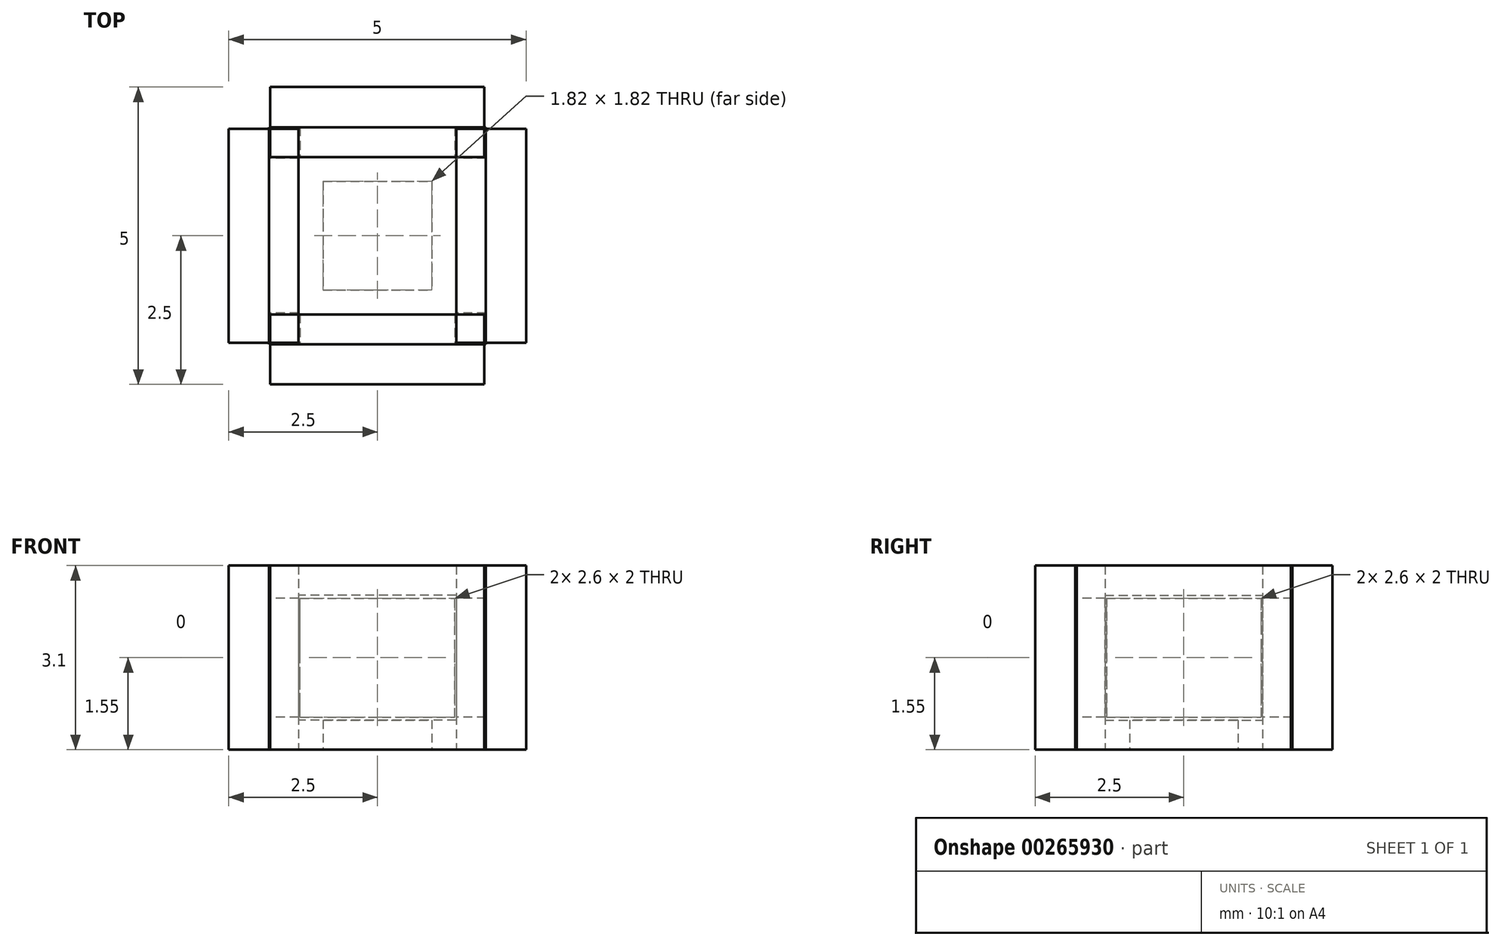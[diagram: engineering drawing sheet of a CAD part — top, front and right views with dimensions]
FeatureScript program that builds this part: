
annotation { "Feature Type Name" : "Feature", "Feature Type Description" : "" }
export const myFeature = defineFeature(function(context is Context, id is Id, definition is map)
    precondition{}
    {
        {
            var Q0;
            Q0=qCreatedBy(makeId("Top.planeOp"),FACE);
            var sketch = newSketch(context, id + "F0", { "sketchPlane" : qUnion([Q0])});
            skLineSegment(sketch, "E0.bottom", {"start": v(1.82, -1.82) * mm, "end": v(-1.82, -1.83) * mm});
            skLineSegment(sketch, "E0.top", {"start": v(1.83, 1.83) * mm, "end": v(-1.82, 1.82) * mm});
            skLineSegment(sketch, "E0.left", {"start": v(1.82, -1.82) * mm, "end": v(1.83, 1.83) * mm});
            skLineSegment(sketch, "E0.right", {"start": v(-1.82, -1.83) * mm, "end": v(-1.82, 1.82) * mm});
            skPoint(sketch, "E0.middle", {"position": v(0, 0) * mm});
            skSolve(sketch);
        }
        {
            var Q0;
            Q0=qSketchRegion(id+"F0",true);
            extrude(context, id + "F1", {"entities" : qUnion([Q0]), "depth" : 3.1 * mm});
        }
        {
            var Q0;
            Q0=qCreatedBy(makeId("Top.planeOp"),FACE);
            var sketch = newSketch(context, id + "F2", { "sketchPlane" : qUnion([Q0])});
            skLineSegment(sketch, "E1.bottom", {"start": v(1.33, -1.32) * mm, "end": v(-1.32, -1.32) * mm});
            skLineSegment(sketch, "E1.top", {"start": v(1.32, 1.32) * mm, "end": v(-1.33, 1.32) * mm});
            skLineSegment(sketch, "E1.left", {"start": v(1.32, -1.32) * mm, "end": v(1.32, 1.33) * mm});
            skLineSegment(sketch, "E1.right", {"start": v(-1.32, -1.32) * mm, "end": v(-1.33, 1.33) * mm});
            skPoint(sketch, "E1.middle", {"position": v(0, 0) * mm});
            skSolve(sketch);
        }
        {
            var Q0;
            Q0=qSketchRegion(id+"F2",true);
            extrude(context, id + "F3", {"entities" : qUnion([Q0]), "depth" : 2.1 * mm});
        }
        {
            var Q0;
            Q0=makeQuery(id+"F3.opExtrude","SWEPT_BODY",BODY,{"disambiguationData":[OSD([sQuery(id+"F2.wireOp",EDGE,"E1.bottom"),sQuery(id+"F2.wireOp",EDGE,"E1.top"),sQuery(id+"F2.wireOp",EDGE,"E1.left"),sQuery(id+"F2.wireOp",EDGE,"E1.right")])]});
            transform(context, id + "F4", {"entities" : qUnion([Q0]), "transformType" : TransformType.TRANSLATION_3D, "dx" : 0 * mm, "dy" : 0 * mm, "dz" : 0.5 * mm, "makeCopy" : false});
        }
        {
            var Q0;
            Q0=qCreatedBy(makeId("Top.planeOp"),FACE);
            var sketch = newSketch(context, id + "F5", { "sketchPlane" : qUnion([Q0])});
            skLineSegment(sketch, "E2.bottom", {"start": v(0.91, -0.91) * mm, "end": v(-0.91, -0.91) * mm});
            skLineSegment(sketch, "E2.top", {"start": v(0.91, 0.91) * mm, "end": v(-0.91, 0.91) * mm});
            skLineSegment(sketch, "E2.left", {"start": v(0.91, -0.91) * mm, "end": v(0.91, 0.91) * mm});
            skLineSegment(sketch, "E2.right", {"start": v(-0.91, -0.91) * mm, "end": v(-0.91, 0.91) * mm});
            skPoint(sketch, "E2.middle", {"position": v(0, 0) * mm});
            skSolve(sketch);
        }
        {
            var Q0;
            Q0=qSketchRegion(id+"F5",true);
            extrude(context, id + "F6", {"entities" : qUnion([Q0]), "operationType" : NewBodyOperationType.REMOVE, "depth" : 2.6 * mm});
        }
        {
            var Q0;
            Q0=makeQuery(id+"F3.opExtrude","SWEPT_BODY",BODY,{"disambiguationData":[OSD([sQuery(id+"F2.wireOp",EDGE,"E1.bottom"),sQuery(id+"F2.wireOp",EDGE,"E1.top"),sQuery(id+"F2.wireOp",EDGE,"E1.left"),sQuery(id+"F2.wireOp",EDGE,"E1.right")])]});
            var Q1;
            Q1=makeQuery(id+"F1.opExtrude","SWEPT_BODY",BODY,{"disambiguationData":[OSD([sQuery(id+"F0.wireOp",EDGE,"E0.bottom"),sQuery(id+"F0.wireOp",EDGE,"E0.top"),sQuery(id+"F0.wireOp",EDGE,"E0.left"),sQuery(id+"F0.wireOp",EDGE,"E0.right")])]});
            booleanBodies(context, id + "F7", {"operationType" : BooleanOperationType.SUBTRACTION, "tools" : qUnion([Q0]), "targets" : qUnion([Q1])});
        }
        {
            var Q0;
            Q0=qCreatedBy(makeId("Front.planeOp"),FACE);
            var sketch = newSketch(context, id + "F8", { "sketchPlane" : qUnion([Q0])});
            skPoint(sketch, "E3.middle", {"position": v(0, 0) * mm});
            skLineSegment(sketch, "E4.bottom", {"start": v(-1.3, -1) * mm, "end": v(1.3, -1) * mm});
            skLineSegment(sketch, "E4.top", {"start": v(-1.3, 1) * mm, "end": v(1.3, 1) * mm});
            skLineSegment(sketch, "E4.left", {"start": v(-1.3, -1) * mm, "end": v(-1.3, 1) * mm});
            skLineSegment(sketch, "E4.right", {"start": v(1.3, -1) * mm, "end": v(1.3, 1) * mm});
            skSolve(sketch);
        }
        {
            var Q0;
            Q0 = qSketchRegion(id + "F8", true);
            extrude(context, id + "F9", {"entities" : qUnion([Q0]), "oppositeDirection" : true, "depth" : 1.18 * mm});
        }
        {
            var Q0;
            Q0=makeQuery(id+"F9.opExtrude","SWEPT_BODY",BODY,{"disambiguationData":[OSD([sQuery(id+"F8.wireOp",EDGE,"E4.bottom"),sQuery(id+"F8.wireOp",EDGE,"E4.top"),sQuery(id+"F8.wireOp",EDGE,"E4.left"),sQuery(id+"F8.wireOp",EDGE,"E4.right")])]});
            transform(context, id + "F10", {"entities" : qUnion([Q0]), "transformType" : TransformType.TRANSLATION_3D, "dx" : 0 * mm, "dy" : 1.32 * mm, "dz" : 1.55 * mm, "makeCopy" : false});
        }
        {
            var Q0;
            Q0=makeQuery(id+"F9.opExtrude","SWEPT_BODY",BODY,{"disambiguationData":[OSD([sQuery(id+"F8.wireOp",EDGE,"E4.bottom"),sQuery(id+"F8.wireOp",EDGE,"E4.top"),sQuery(id+"F8.wireOp",EDGE,"E4.left"),sQuery(id+"F8.wireOp",EDGE,"E4.right")])]});
            var Q1;
            Q1=makeQuery(id+"F7.opBoolean","COPY",EDGE,{"derivedFrom":makeQuery(id+"F3.opExtrude","SWEPT_EDGE",EDGE,{"disambiguationData":[OSD([sQuery(id+"F2.wireOp",EDGE,"E1.top"),sQuery(id+"F2.wireOp",EDGE,"E1.left")])]})});
            transform(context, id + "F11", {"entities" : qUnion([Q0]), "transformType" : TransformType.TRANSLATION_3D, "dx" : 0 * mm, "dy" : -3.83 * mm, "dz" : 0 * mm, "makeCopy" : true});
        }
        {
            var Q0;
            Q0=qCreatedBy(makeId("Right.planeOp"),FACE);
            var sketch = newSketch(context, id + "F12", { "sketchPlane" : qUnion([Q0])});
            skPoint(sketch, "E5.middle", {"position": v(0, 0) * mm});
            skLineSegment(sketch, "E6.bottom", {"start": v(-1.3, 1) * mm, "end": v(1.3, 1) * mm});
            skLineSegment(sketch, "E6.top", {"start": v(-1.3, -1) * mm, "end": v(1.3, -1) * mm});
            skLineSegment(sketch, "E6.left", {"start": v(-1.3, 1) * mm, "end": v(-1.3, -1) * mm});
            skLineSegment(sketch, "E6.right", {"start": v(1.3, 1) * mm, "end": v(1.3, -1) * mm});
            skSolve(sketch);
        }
        {
            var Q0;
            Q0=qSketchRegion(id+"F12",true);
            extrude(context, id + "F13", {"entities" : qUnion([Q0]), "depth" : 1.18 * mm});
        }
        {
            var Q0;
            Q0=makeQuery(id+"F13.opExtrude","SWEPT_BODY",BODY,{"disambiguationData":[OSD([sQuery(id+"F12.wireOp",EDGE,"E6.bottom"),sQuery(id+"F12.wireOp",EDGE,"E6.top"),sQuery(id+"F12.wireOp",EDGE,"E6.left"),sQuery(id+"F12.wireOp",EDGE,"E6.right")])]});
            transform(context, id + "F14", {"entities" : qUnion([Q0]), "transformType" : TransformType.TRANSLATION_3D, "dx" : 1.32 * mm, "dy" : 0 * mm, "dz" : 1.55 * mm, "makeCopy" : false});
        }
        {
            var Q0;
            Q0=makeQuery(id+"F13.opExtrude","SWEPT_BODY",BODY,{"disambiguationData":[OSD([sQuery(id+"F12.wireOp",EDGE,"E6.bottom"),sQuery(id+"F12.wireOp",EDGE,"E6.top"),sQuery(id+"F12.wireOp",EDGE,"E6.left"),sQuery(id+"F12.wireOp",EDGE,"E6.right")])]});
            transform(context, id + "F15", {"entities" : qUnion([Q0]), "transformType" : TransformType.TRANSLATION_3D, "dx" : -3.83 * mm, "dy" : 0 * mm, "dz" : 0 * mm, "makeCopy" : true});
        }
        {
            var Q0;
            Q0=qCreatedBy(makeId("Right.planeOp"),FACE);
            var sketch = newSketch(context, id + "F16", { "sketchPlane" : qUnion([Q0])});
            skLineSegment(sketch, "E7.bottom", {"start": v(1.8, 1.55) * mm, "end": v(-1.8, 1.55) * mm});
            skLineSegment(sketch, "E7.top", {"start": v(1.8, -1.55) * mm, "end": v(-1.8, -1.55) * mm});
            skLineSegment(sketch, "E7.left", {"start": v(1.8, 1.55) * mm, "end": v(1.8, -1.55) * mm});
            skLineSegment(sketch, "E7.right", {"start": v(-1.8, 1.55) * mm, "end": v(-1.8, -1.55) * mm});
            skPoint(sketch, "E7.middle", {"position": v(0, 0) * mm});
            skSolve(sketch);
        }
        {
            var Q0;
            Q0=qSketchRegion(id+"F16",true);
            extrude(context, id + "F17", {"entities" : qUnion([Q0]), "depth" : 1.18 * mm});
        }
        {
            var Q0;
            Q0=makeQuery(id+"F17.opExtrude","SWEPT_BODY",BODY,{"disambiguationData":[OSD([sQuery(id+"F16.wireOp",EDGE,"E7.bottom"),sQuery(id+"F16.wireOp",EDGE,"E7.top"),sQuery(id+"F16.wireOp",EDGE,"E7.left"),sQuery(id+"F16.wireOp",EDGE,"E7.right")])]});
            transform(context, id + "F18", {"entities" : qUnion([Q0]), "transformType" : TransformType.TRANSLATION_3D, "dx" : 1.32 * mm, "dy" : 0 * mm, "dz" : 1.55 * mm, "makeCopy" : false});
        }
        {
            var Q0;
            Q0=makeQuery(id+"F17.opExtrude","SWEPT_BODY",BODY,{"disambiguationData":[OSD([sQuery(id+"F16.wireOp",EDGE,"E7.bottom"),sQuery(id+"F16.wireOp",EDGE,"E7.top"),sQuery(id+"F16.wireOp",EDGE,"E7.left"),sQuery(id+"F16.wireOp",EDGE,"E7.right")])]});
            transform(context, id + "F19", {"entities" : qUnion([Q0]), "transformType" : TransformType.TRANSLATION_3D, "dx" : -3.83 * mm, "dy" : 0 * mm, "dz" : 0 * mm, "makeCopy" : true});
        }
        {
            var Q0;
            Q0=qCreatedBy(makeId("Front.planeOp"),FACE);
            var sketch = newSketch(context, id + "F20", { "sketchPlane" : qUnion([Q0])});
            skLineSegment(sketch, "E8.bottom", {"start": v(1.8, 1.55) * mm, "end": v(-1.8, 1.55) * mm});
            skLineSegment(sketch, "E8.top", {"start": v(1.8, -1.55) * mm, "end": v(-1.8, -1.55) * mm});
            skLineSegment(sketch, "E8.left", {"start": v(1.8, 1.55) * mm, "end": v(1.8, -1.55) * mm});
            skLineSegment(sketch, "E8.right", {"start": v(-1.8, 1.55) * mm, "end": v(-1.8, -1.55) * mm});
            skPoint(sketch, "E8.middle", {"position": v(0, 0) * mm});
            skSolve(sketch);
        }
        {
            var Q0;
            Q0=qSketchRegion(id+"F20",true);
            extrude(context, id + "F21", {"entities" : qUnion([Q0]), "depth" : 1.18 * mm});
        }
        {
            var Q0;
            Q0=makeQuery(id+"F21.opExtrude","SWEPT_BODY",BODY,{"disambiguationData":[OSD([sQuery(id+"F20.wireOp",EDGE,"E8.bottom"),sQuery(id+"F20.wireOp",EDGE,"E8.top"),sQuery(id+"F20.wireOp",EDGE,"E8.left"),sQuery(id+"F20.wireOp",EDGE,"E8.right")])]});
            transform(context, id + "F22", {"entities" : qUnion([Q0]), "transformType" : TransformType.TRANSLATION_3D, "dx" : 0 * mm, "dy" : -1.32 * mm, "dz" : 1.55 * mm, "makeCopy" : false});
        }
        {
            var Q0;
            Q0=makeQuery(id+"F21.opExtrude","SWEPT_BODY",BODY,{"disambiguationData":[OSD([sQuery(id+"F20.wireOp",EDGE,"E8.bottom"),sQuery(id+"F20.wireOp",EDGE,"E8.top"),sQuery(id+"F20.wireOp",EDGE,"E8.left"),sQuery(id+"F20.wireOp",EDGE,"E8.right")])]});
            transform(context, id + "F23", {"entities" : qUnion([Q0]), "transformType" : TransformType.TRANSLATION_3D, "dx" : 0 * mm, "dy" : 3.83 * mm, "dz" : 0 * mm, "makeCopy" : true});
        }
        {
            var Q0;
            Q0=makeQuery(id+"F9.opExtrude","SWEPT_BODY",BODY,{"disambiguationData":[OSD([sQuery(id+"F8.wireOp",EDGE,"E4.bottom"),sQuery(id+"F8.wireOp",EDGE,"E4.top"),sQuery(id+"F8.wireOp",EDGE,"E4.left"),sQuery(id+"F8.wireOp",EDGE,"E4.right")])]});
            var Q1;
            Q1=makeQuery(id+"F13.opExtrude","SWEPT_BODY",BODY,{"disambiguationData":[OSD([sQuery(id+"F12.wireOp",EDGE,"E6.bottom"),sQuery(id+"F12.wireOp",EDGE,"E6.top"),sQuery(id+"F12.wireOp",EDGE,"E6.left"),sQuery(id+"F12.wireOp",EDGE,"E6.right")])]});
            var Q2;
            Q2=makeQuery(id+"F11.opPattern","COPY",BODY,{"derivedFrom":makeQuery(id+"F9.opExtrude","SWEPT_BODY",BODY,{"disambiguationData":[OSD([sQuery(id+"F8.wireOp",EDGE,"E4.bottom"),sQuery(id+"F8.wireOp",EDGE,"E4.top"),sQuery(id+"F8.wireOp",EDGE,"E4.left"),sQuery(id+"F8.wireOp",EDGE,"E4.right")])]}),"instanceName":"1"});
            var Q3;
            Q3=makeQuery(id+"F15.opPattern","COPY",BODY,{"derivedFrom":makeQuery(id+"F13.opExtrude","SWEPT_BODY",BODY,{"disambiguationData":[OSD([sQuery(id+"F12.wireOp",EDGE,"E6.bottom"),sQuery(id+"F12.wireOp",EDGE,"E6.top"),sQuery(id+"F12.wireOp",EDGE,"E6.left"),sQuery(id+"F12.wireOp",EDGE,"E6.right")])]}),"instanceName":"1"});
            var Q4;
            Q4=makeQuery(id+"F1.opExtrude","SWEPT_BODY",BODY,{"disambiguationData":[OSD([sQuery(id+"F0.wireOp",EDGE,"E0.bottom"),sQuery(id+"F0.wireOp",EDGE,"E0.top"),sQuery(id+"F0.wireOp",EDGE,"E0.left"),sQuery(id+"F0.wireOp",EDGE,"E0.right")])]});
            booleanBodies(context, id + "F24", {"operationType" : BooleanOperationType.SUBTRACTION, "tools" : qUnion([Q0, Q1, Q2, Q3]), "targets" : qUnion([Q4])});
        }
    });
